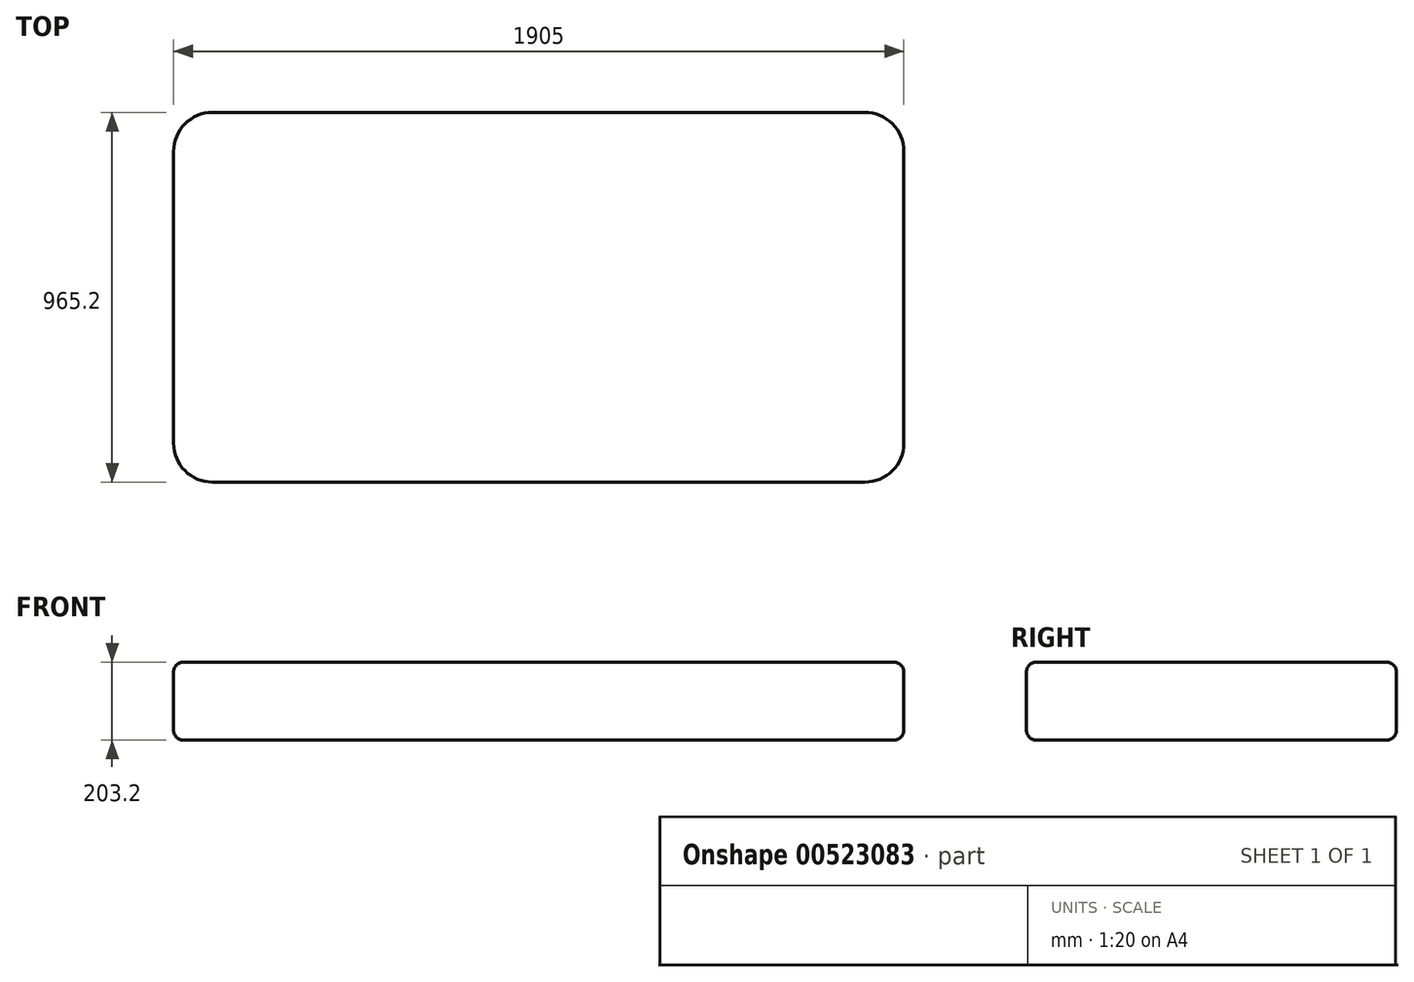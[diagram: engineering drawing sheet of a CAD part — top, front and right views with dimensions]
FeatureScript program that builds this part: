
annotation { "Feature Type Name" : "Feature", "Feature Type Description" : "" }
export const myFeature = defineFeature(function(context is Context, id is Id, definition is map)
    precondition{}
    {
        {
            var Q0;
            Q0=qCreatedBy(makeId("Top.planeOp"),FACE);
            var sketch = newSketch(context, id + "F0", { "sketchPlane" : qUnion([Q0])});
            skLineSegment(sketch, "E0.bottom", {"start": v(0, 0) * mm, "end": v(1905, 0) * mm});
            skLineSegment(sketch, "E0.top", {"start": v(0, 965.2) * mm, "end": v(1905, 965.2) * mm});
            skLineSegment(sketch, "E0.left", {"start": v(0, 0) * mm, "end": v(0, 965.2) * mm});
            skLineSegment(sketch, "E0.right", {"start": v(1905, 0) * mm, "end": v(1905, 965.2) * mm});
            skSolve(sketch);
        }
        {
            var Q0;
            Q0 = qSketchRegion(id + "F0", true);
            extrude(context, id + "F1", {"entities" : qUnion([Q0]), "depth" : 203.2 * mm, "offsetDistance" : 25.4 * mm});
        }
        {
            var Q0;
            Q0=makeQuery(id+"F1.opExtrude","SWEPT_EDGE",EDGE,{"disambiguationData":[OSD([sQuery(id+"F0.wireOp",EDGE,"E0.bottom"),sQuery(id+"F0.wireOp",EDGE,"E0.left")])]});
            var Q1;
            Q1=makeQuery(id+"F1.opExtrude","SWEPT_EDGE",EDGE,{"disambiguationData":[OSD([sQuery(id+"F0.wireOp",EDGE,"E0.top"),sQuery(id+"F0.wireOp",EDGE,"E0.left")])]});
            var Q2;
            Q2=makeQuery(id+"F1.opExtrude","SWEPT_EDGE",EDGE,{"disambiguationData":[OSD([sQuery(id+"F0.wireOp",EDGE,"E0.bottom"),sQuery(id+"F0.wireOp",EDGE,"E0.right")])]});
            var Q3;
            Q3=makeQuery(id+"F1.opExtrude","SWEPT_EDGE",EDGE,{"disambiguationData":[OSD([sQuery(id+"F0.wireOp",EDGE,"E0.top"),sQuery(id+"F0.wireOp",EDGE,"E0.right")])]});
            fillet(context, id + "F2", {"entities" : qUnion([Q0, Q1, Q2, Q3]), "radius" : 101.6 * mm, "tangentPropagation" : true, "allowEdgeOverflow" : false});
        }
        {
            var Q0;
            Q0=makeQuery(id+"F1.opExtrude","CAP_FACE",FACE,{"disambiguationData":[OSD([sQuery(id+"F0.wireOp",EDGE,"E0.bottom"),sQuery(id+"F0.wireOp",EDGE,"E0.top"),sQuery(id+"F0.wireOp",EDGE,"E0.left"),sQuery(id+"F0.wireOp",EDGE,"E0.right")])],"isStart":false});
            fillet(context, id + "F3", {"entities" : qUnion([Q0]), "radius" : 25.4 * mm, "tangentPropagation" : true, "allowEdgeOverflow" : false});
        }
        {
            var Q0;
            Q0=makeQuery(id+"F1.opExtrude","CAP_FACE",FACE,{"disambiguationData":[OSD([sQuery(id+"F0.wireOp",EDGE,"E0.bottom"),sQuery(id+"F0.wireOp",EDGE,"E0.top"),sQuery(id+"F0.wireOp",EDGE,"E0.left"),sQuery(id+"F0.wireOp",EDGE,"E0.right")])],"isStart":true});
            fillet(context, id + "F4", {"entities" : qUnion([Q0]), "radius" : 25.4 * mm, "tangentPropagation" : true, "allowEdgeOverflow" : false});
        }
    });
